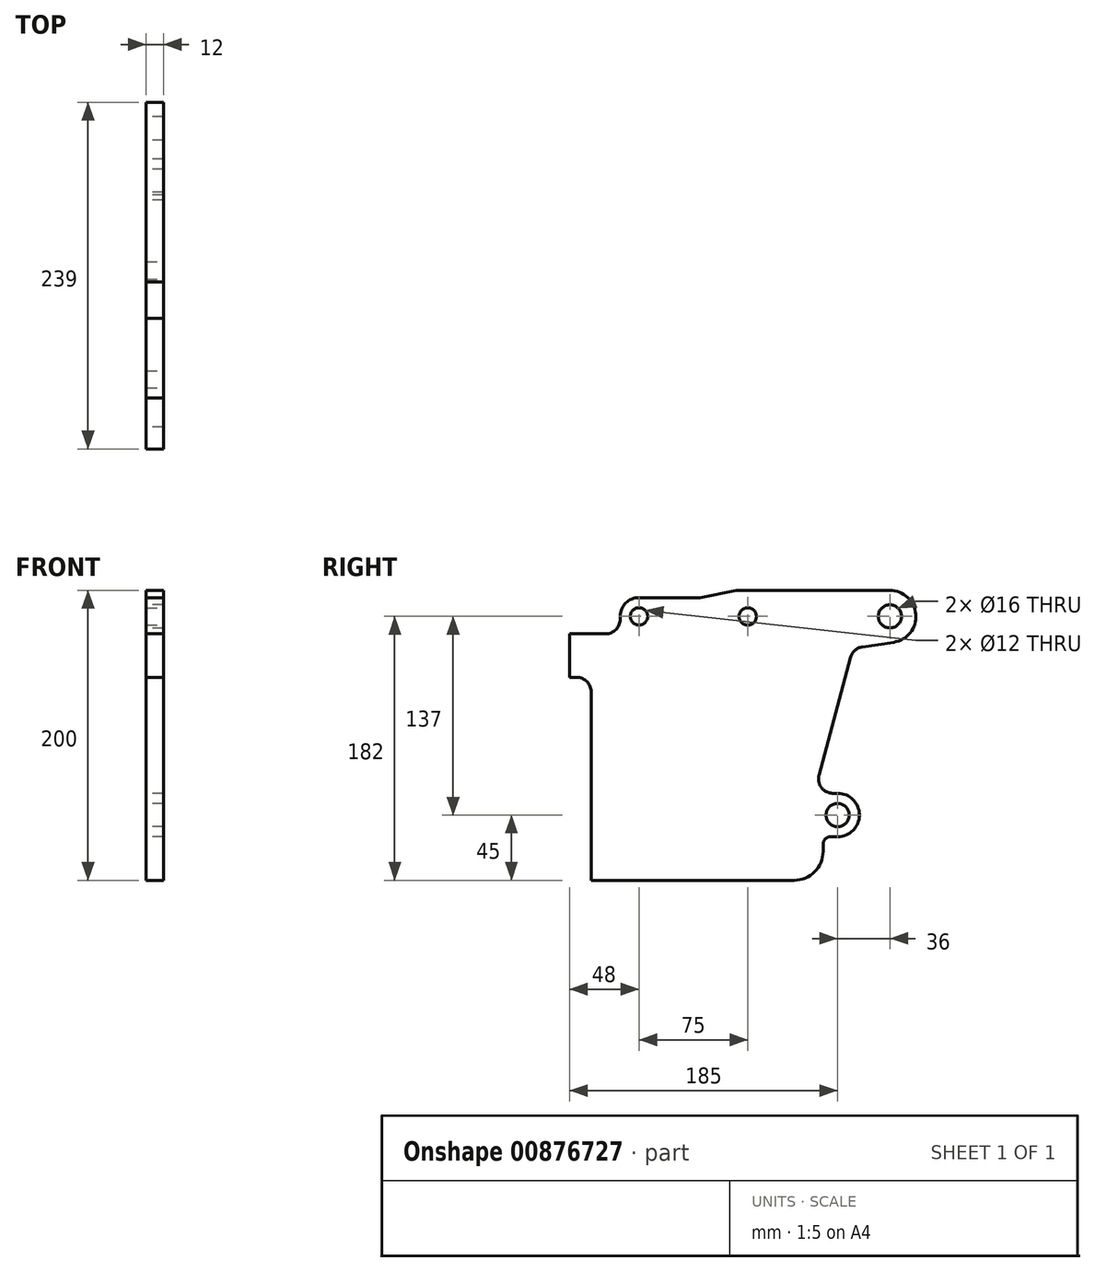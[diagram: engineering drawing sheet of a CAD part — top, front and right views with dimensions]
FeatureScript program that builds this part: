
annotation { "Feature Type Name" : "Feature", "Feature Type Description" : "" }
export const myFeature = defineFeature(function(context is Context, id is Id, definition is map)
    precondition{}
    {
        {
            var Q0;
            Q0=qCreatedBy(makeId("Right.planeOp"),FACE);
            var sketch = newSketch(context, id + "F0", { "sketchPlane" : qUnion([Q0])});
            skLineSegment(sketch, "E0.bottom", {"start": v(50, 170) * mm, "end": v(200, 170) * mm, "construction": true});
            skLineSegment(sketch, "E0.top", {"start": v(50, 160) * mm, "end": v(200, 160) * mm, "construction": true});
            skLineSegment(sketch, "E0.left", {"start": v(50, 170) * mm, "end": v(50, 160) * mm, "construction": true});
            skLineSegment(sketch, "E0.right", {"start": v(200, 170) * mm, "end": v(200, 160) * mm, "construction": true});
            skLineSegment(sketch, "E1", {"start": v(165, 160) * mm, "end": v(126.18, 15.11) * mm, "construction": true});
            skLineSegment(sketch, "E2", {"start": v(126.18, 15.11) * mm, "end": v(135.84, 12.52) * mm, "construction": true});
            skLineSegment(sketch, "E3", {"start": v(135.84, 12.52) * mm, "end": v(174.66, 157.41) * mm, "construction": true});
            skLineSegment(sketch, "E4", {"start": v(174.66, 157.41) * mm, "end": v(165, 160) * mm, "construction": true});
            skLineSegment(sketch, "E5", {"start": v(0, 0) * mm, "end": v(0, 130) * mm});
            skLineSegment(sketch, "E6", {"start": v(-10, 140) * mm, "end": v(-15, 140) * mm});
            skLineSegment(sketch, "E7", {"start": v(-15, 140) * mm, "end": v(-15, 170) * mm});
            skLineSegment(sketch, "E8", {"start": v(-15, 170) * mm, "end": v(10, 170) * mm});
            skLineSegment(sketch, "E9", {"start": v(20, 180) * mm, "end": v(20, 182) * mm});
            skLineSegment(sketch, "E10", {"start": v(33, 195) * mm, "end": v(75, 195) * mm});
            skLineSegment(sketch, "E11", {"start": v(75, 195) * mm, "end": v(100, 200) * mm});
            skLineSegment(sketch, "E12", {"start": v(100, 200) * mm, "end": v(206, 200) * mm});
            skLineSegment(sketch, "E13", {"start": v(208.66, 164.2) * mm, "end": v(187.02, 160.97) * mm});
            skLineSegment(sketch, "E14", {"start": v(178.83, 153.67) * mm, "end": v(157.1, 72.59) * mm});
            skLineSegment(sketch, "E15", {"start": v(160, 25) * mm, "end": v(160, 20) * mm});
            skLineSegment(sketch, "E16", {"start": v(140, 0) * mm, "end": v(0, 0) * mm});
            skArc(sketch, "E17", {"start": v(208.66, 164.2) * mm, "mid": v(223.95, 183.33) * mm, "end": v(206, 200) * mm});
            skLineSegment(sketch, "E18", {"start": v(165, 30) * mm, "end": v(170, 30) * mm});
            skArc(sketch, "E19", {"start": v(170, 30) * mm, "mid": v(185, 45) * mm, "end": v(170, 60) * mm});
            skLineSegment(sketch, "E20", {"start": v(166.77, 60) * mm, "end": v(170, 60) * mm});
            skPoint(sketch, "E21.visualSharp", {"position": v(160, 0) * mm});
            skArc(sketch, "E21.filletArc", {"start": v(140, 0) * mm, "mid": v(154.14, 5.86) * mm, "end": v(160, 20) * mm});
            skPoint(sketch, "E22.visualSharp", {"position": v(153.73, 60) * mm});
            skArc(sketch, "E22.filletArc", {"start": v(157.1, 72.59) * mm, "mid": v(158.83, 63.91) * mm, "end": v(166.77, 60) * mm});
            skArc(sketch, "E23.filletArc", {"start": v(187.02, 160.97) * mm, "mid": v(181.83, 158.54) * mm, "end": v(178.83, 153.67) * mm});
            skPoint(sketch, "E24.visualSharp", {"position": v(20, 195) * mm});
            skArc(sketch, "E24.filletArc", {"start": v(33, 195) * mm, "mid": v(23.8, 191.2) * mm, "end": v(20, 182) * mm});
            skPoint(sketch, "E25.visualSharp", {"position": v(20, 170) * mm});
            skArc(sketch, "E25.filletArc", {"start": v(10, 170) * mm, "mid": v(17.07, 172.93) * mm, "end": v(20, 180) * mm});
            skPoint(sketch, "E26.visualSharp", {"position": v(0, 140) * mm});
            skArc(sketch, "E26.filletArc", {"start": v(0, 130) * mm, "mid": v(-2.93, 137.07) * mm, "end": v(-10, 140) * mm});
            skPoint(sketch, "E27.visualSharp", {"position": v(160, 30) * mm});
            skArc(sketch, "E27.filletArc", {"start": v(165, 30) * mm, "mid": v(161.46, 28.54) * mm, "end": v(160, 25) * mm});
            skCircle(sketch, "E28", {"center": v(206, 182) * mm, "radius": 8 * mm});
            skCircle(sketch, "E29", {"center": v(170, 45) * mm, "radius": 8 * mm});
            skSolve(sketch);
        }
        {
            var Q0;
            Q0=makeQuery(id+"F0.imprint","IMPRINT",FACE,{"disambiguationData":[TD([[makeQuery(id+"F0.imprint","IMPRINT",EDGE,{"derivedFrom":sQuery(id+"F0.wireOp",EDGE,"E5")}),-1.0]])]});
            extrude(context, id + "F1", {"entities" : qUnion([Q0]), "depth" : 12 * mm, "offsetDistance" : 25 * mm});
        }
        {
            var Q0;
            Q0=makeQuery(id+"F1.opExtrude","CAP_FACE",FACE,{"disambiguationData":[OSD([sQuery(id+"F0.wireOp",EDGE,"E5"),sQuery(id+"F0.wireOp",EDGE,"E7"),sQuery(id+"F0.wireOp",EDGE,"E8"),sQuery(id+"F0.wireOp",EDGE,"E9"),sQuery(id+"F0.wireOp",EDGE,"E10"),sQuery(id+"F0.wireOp",EDGE,"E11"),sQuery(id+"F0.wireOp",EDGE,"E12"),sQuery(id+"F0.wireOp",EDGE,"E13"),sQuery(id+"F0.wireOp",EDGE,"E14"),sQuery(id+"F0.wireOp",EDGE,"E15"),sQuery(id+"F0.wireOp",EDGE,"E16"),sQuery(id+"F0.wireOp",EDGE,"E17"),sQuery(id+"F0.wireOp",EDGE,"E18"),sQuery(id+"F0.wireOp",EDGE,"E19"),sQuery(id+"F0.wireOp",EDGE,"E20"),sQuery(id+"F0.wireOp",EDGE,"E21.filletArc"),sQuery(id+"F0.wireOp",EDGE,"E22.filletArc"),sQuery(id+"F0.wireOp",EDGE,"E23.filletArc"),sQuery(id+"F0.wireOp",EDGE,"E24.filletArc"),sQuery(id+"F0.wireOp",EDGE,"E25.filletArc"),sQuery(id+"F0.wireOp",EDGE,"E26.filletArc"),sQuery(id+"F0.wireOp",EDGE,"E27.filletArc"),sQuery(id+"F0.wireOp",EDGE,"E28"),sQuery(id+"F0.wireOp",EDGE,"E29")])],"isStart":false});
            var sketch = newSketch(context, id + "F2", { "sketchPlane" : qUnion([Q0])});
            skLineSegment(sketch, "E30", {"start": v(206, 182) * mm, "end": v(0, 182) * mm, "construction": true});
            skPoint(sketch, "E31", {"position": v(33, 182) * mm});
            skPoint(sketch, "E32", {"position": v(108, 182) * mm});
            skSolve(sketch);
        }
        {
            var Q0;
            Q0=sQuery(id+"F2.wireOp",VERTEX,"E31");
            var Q1;
            Q1=sQuery(id+"F2.wireOp",VERTEX,"E32");
            var Q2;
            Q2=makeQuery(id+"F1.opExtrude","SWEPT_BODY",BODY,{"disambiguationData":[OSD([sQuery(id+"F0.wireOp",EDGE,"E5"),sQuery(id+"F0.wireOp",EDGE,"E7"),sQuery(id+"F0.wireOp",EDGE,"E8"),sQuery(id+"F0.wireOp",EDGE,"E9"),sQuery(id+"F0.wireOp",EDGE,"E10"),sQuery(id+"F0.wireOp",EDGE,"E11"),sQuery(id+"F0.wireOp",EDGE,"E12"),sQuery(id+"F0.wireOp",EDGE,"E13"),sQuery(id+"F0.wireOp",EDGE,"E14"),sQuery(id+"F0.wireOp",EDGE,"E15"),sQuery(id+"F0.wireOp",EDGE,"E16"),sQuery(id+"F0.wireOp",EDGE,"E17"),sQuery(id+"F0.wireOp",EDGE,"E18"),sQuery(id+"F0.wireOp",EDGE,"E19"),sQuery(id+"F0.wireOp",EDGE,"E20"),sQuery(id+"F0.wireOp",EDGE,"E21.filletArc"),sQuery(id+"F0.wireOp",EDGE,"E22.filletArc"),sQuery(id+"F0.wireOp",EDGE,"E23.filletArc"),sQuery(id+"F0.wireOp",EDGE,"E24.filletArc"),sQuery(id+"F0.wireOp",EDGE,"E25.filletArc"),sQuery(id+"F0.wireOp",EDGE,"E26.filletArc"),sQuery(id+"F0.wireOp",EDGE,"E27.filletArc"),sQuery(id+"F0.wireOp",EDGE,"E28"),sQuery(id+"F0.wireOp",EDGE,"E29")])]});
            hole(context, id + "F3", {"style" : HoleStyle.SIMPLE, "endStyle" : HoleEndStyle.THROUGH, "holeDiameter" : 12 * mm, "majorDiameter" : 5 * mm, "isTappedThrough" : true, "tappedDepth" : 12 * mm, "tapClearance" : 3, "locations" : qUnion([Q0, Q1]), "scope" : qUnion([Q2])});
        }
    });
